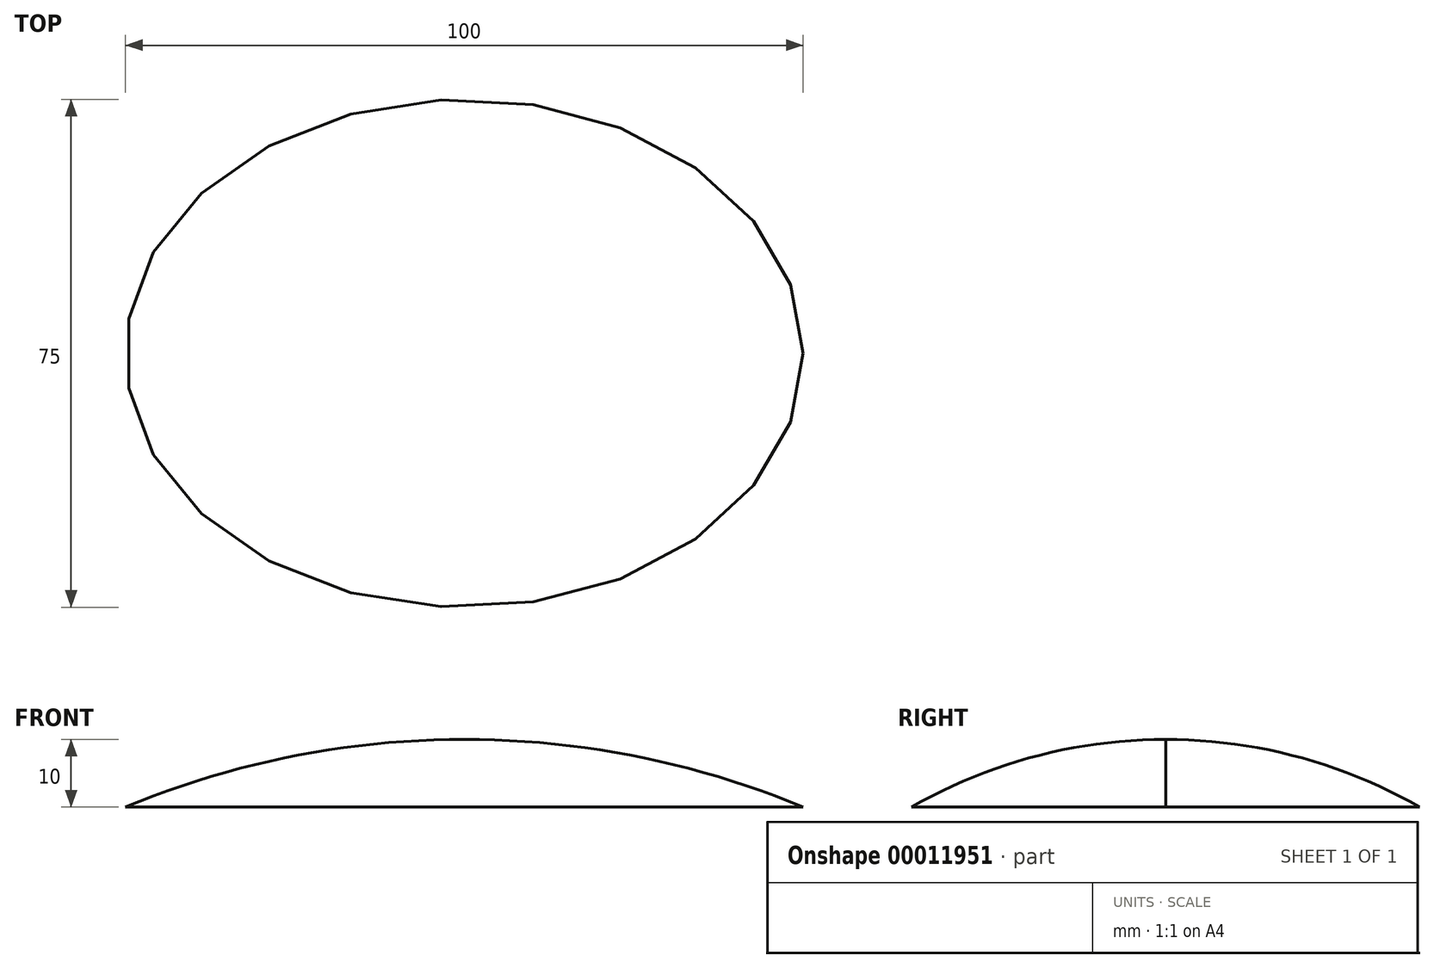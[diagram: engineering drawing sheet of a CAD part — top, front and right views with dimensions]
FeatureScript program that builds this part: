
annotation { "Feature Type Name" : "Feature", "Feature Type Description" : "" }
export const myFeature = defineFeature(function(context is Context, id is Id, definition is map)
    precondition{}
    {
        {
            var Q0;
            Q0=qCreatedBy(makeId("Top.planeOp"),FACE);
            var sketch = newSketch(context, id + "F0", { "sketchPlane" : qUnion([Q0])});
            skLineSegment(sketch, "E0", {"start": v(0, 0) * mm, "end": v(50, 0) * mm, "construction": true});
            skLineSegment(sketch, "E1", {"start": v(0, 0) * mm, "end": v(0, 37.5) * mm, "construction": true});
            skEllipse(sketch, "E2", {"center": v(0, 0) * mm, "majorRadius": 50 * mm, "minorRadius": 37.5 * mm, "majorAxis": v(1, 0)});
            skSolve(sketch);
        }
        {
            var Q0;
            Q0=qCreatedBy(makeId("Front.planeOp"),FACE);
            var sketch = newSketch(context, id + "F1", { "sketchPlane" : qUnion([Q0])});
            skLineSegment(sketch, "E3", {"start": v(0, 0) * mm, "end": v(0, 10) * mm, "construction": true});
            skArc(sketch, "E4", {"start": v(50, 0) * mm, "mid": v(25.5, 7.48) * mm, "end": v(0, 10) * mm});
            skSolve(sketch);
        }
        {
            var Q0;
            Q0=qCreatedBy(makeId("Right.planeOp"),FACE);
            var sketch = newSketch(context, id + "F2", { "sketchPlane" : qUnion([Q0])});
            skLineSegment(sketch, "E5", {"start": v(0, 0) * mm, "end": v(0, 10) * mm, "construction": true});
            skArc(sketch, "E6", {"start": v(37.5, 0) * mm, "mid": v(19.4, 7.46) * mm, "end": v(0, 10) * mm});
            skSolve(sketch);
        }
        {
            var Q0;
            Q0=qCreatedBy(makeId("Front.planeOp"),FACE);
            var sketch = newSketch(context, id + "F3", { "sketchPlane" : qUnion([Q0])});
            skLineSegment(sketch, "E7.0", {"start": v(0, 0) * mm, "end": v(0, 10) * mm, "construction": true});
            skArc(sketch, "E8.0", {"start": v(50, 0) * mm, "mid": v(25.5, 7.48) * mm, "end": v(0, 10) * mm, "construction": true});
            skLineSegment(sketch, "E9", {"start": v(0, 10) * mm, "end": v(0, 0) * mm, "construction": true});
            skArc(sketch, "E10.0.MirrorCS", {"start": v(-50, 0) * mm, "mid": v(-25.5, 7.48) * mm, "end": v(0, 10) * mm});
            skSolve(sketch);
        }
        {
            var Q0;
            Q0=qCreatedBy(makeId("Right.planeOp"),FACE);
            var sketch = newSketch(context, id + "F4", { "sketchPlane" : qUnion([Q0])});
            skArc(sketch, "E11.0", {"start": v(37.5, 0) * mm, "mid": v(19.4, 7.46) * mm, "end": v(0, 10) * mm, "construction": true});
            skLineSegment(sketch, "E11.1", {"start": v(0, 0) * mm, "end": v(0, 10) * mm, "construction": true});
            skArc(sketch, "E12.0.MirrorCS", {"start": v(-37.5, 0) * mm, "mid": v(-19.4, 7.46) * mm, "end": v(0, 10) * mm});
            skSolve(sketch);
        }
        {
            var Q0;
            Q0=sQuery(id+"F1.wireOp",EDGE,"E4");
            var Q1;
            Q1=sQuery(id+"F2.wireOp",EDGE,"E6");
            var Q2;
            Q2=sQuery(id+"F3.wireOp",EDGE,"E10.0.MirrorCS");
            var Q3;
            Q3=sQuery(id+"F4.wireOp",EDGE,"E12.0.MirrorCS");
            var Q4;
            Q4=sQuery(id+"F0.wireOp",EDGE,"E2");
            var Q5;
            Q5=sQuery(id+"F0.wireOp",VERTEX,"E0.end");
            var Q6;
            Q6=sQuery(id+"F4.wireOp",VERTEX,"09f91b4d-dd68-4e11-8c16-2b60e2509cb8.0.start");
            var Q7;
            Q7=sQuery(id+"F3.wireOp",VERTEX,"05837fb8-1f4e-4c1d-a666-7b2030571829.0.MirrorCS.end");
            var Q8;
            Q8=sQuery(id+"F4.wireOp",VERTEX,"074d9ff6-27a1-46a8-9423-f7ec91c35071.0.MirrorCS.end");
            loft(context, id + "F5", {"bodyType" : ToolBodyType.SURFACE, "addGuides" : true, "wireProfilesArray" : [{ "wireProfileEntities" : qUnion([Q0]) }, { "wireProfileEntities" : qUnion([Q1]) }, { "wireProfileEntities" : qUnion([Q2]) }, { "wireProfileEntities" : qUnion([Q3]) }], "guidesArray" : [{ "guideEntities" : qUnion([Q4]), "guideDerivativeType" : LoftGuideDerivativeType.DEFAULT, "guideDerivativeMagnitude" : 1 }], "connections" : [{ "connectionEntities" : qUnion([Q5, Q6, Q7, Q8]), "connectionEdgeQueries" : qUnion([]), "connectionEdgeParameters" : [] }]});
        }
        {
            var Q0;
            Q0=makeQuery(id+"F5.opLoft","SWEPT_BODY",BODY,{"disambiguationData":[OSD([sQuery(id+"F0.wireOp",EDGE,"E2"),sQuery(id+"F1.wireOp",EDGE,"E4"),sQuery(id+"F2.wireOp",EDGE,"E6"),sQuery(id+"F3.wireOp",EDGE,"E10.0.MirrorCS"),sQuery(id+"F4.wireOp",EDGE,"E12.0.MirrorCS")])]});
            transform(context, id + "F6", {"entities" : qUnion([Q0]), "transformType" : TransformType.COPY});
        }
    });
